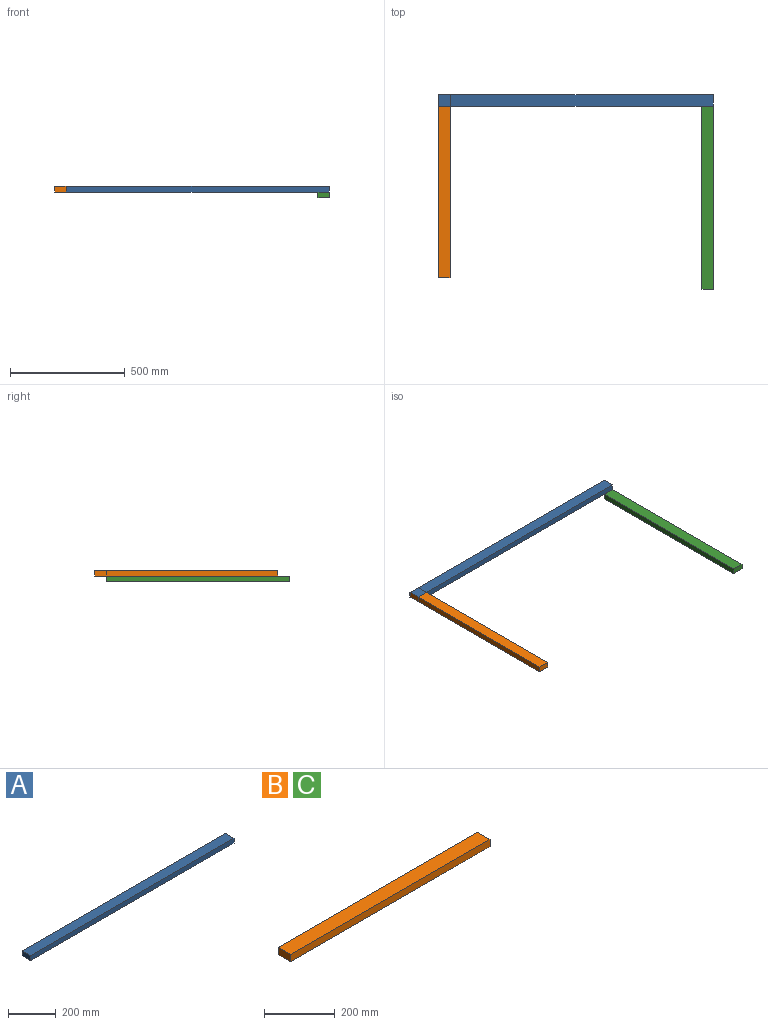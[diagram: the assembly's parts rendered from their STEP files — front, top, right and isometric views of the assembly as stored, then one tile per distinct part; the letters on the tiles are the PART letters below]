
ASSEMBLY  parts=3 mates=3
PART A: 6 faces, bbox 1200x50x25 mm
  f0: plane 1200x50mm, normal (0,0,-1), area 60000mm2, adj f1,f3,f4,f5
  f1: plane 50x25mm, normal (1,0,0), area 1250mm2, adj f0,f2,f4,f5
  f2: plane 1200x50mm, normal (0,0,1), area 60000mm2, adj f1,f3,f4,f5
  f3: plane 50x25mm, normal (-1,0,0), area 1250mm2, adj f0,f2,f4,f5
  f4: plane 1200x25mm, normal (0,-1,0), area 30000mm2, adj f0,f1,f2,f3
  f5: plane 1200x25mm, normal (0,1,0), area 30000mm2, adj f0,f1,f2,f3
PART B: 6 faces, bbox 800x50x25 mm
  f0: plane 50x25mm, normal (1,0,0), area 1250mm2, adj f1,f3,f4,f5
  f1: plane 800x50mm, normal (0,0,1), area 40000mm2, adj f0,f2,f4,f5
  f2: plane 50x25mm, normal (-1,0,0), area 1250mm2, adj f1,f3,f4,f5
  f3: plane 800x50mm, normal (0,0,-1), area 40000mm2, adj f0,f2,f4,f5
  f4: plane 800x25mm, normal (0,-1,0), area 20000mm2, adj f0,f1,f2,f3
  f5: plane 800x25mm, normal (0,1,0), area 20000mm2, adj f0,f1,f2,f3
PART C: same geometry as B
PLACE A t=(-45.31,-525,-45.31)mm fixed
PLACE B rot(axis=(0.71,-0.71,0),180deg) t=(-620.31,-900,-45.31)mm
PLACE C rot(axis=(0,0,-1),90deg) t=(529.69,-950,-70.31)mm
MATE parallel B.f3 <-> A.f3  axis (0,0,-1) through (-595.31,-500,-32.81)mm
MATE planar A.f0 <-> C.f1  axis (0,0,1) through (554.69,-550,-57.81)mm
MATE planar B.f1 <-> A.f0  axis (0,0,-1) through (-645.31,-500,-57.81)mm
